# Revit family: Nivellierbare Kassette mit Schnurauslass, RKSNUZD3, 20-25, 9
name_source: partatom
category: Generic Models
revit_build: Autodesk Revit 2015 (Build: 20140606_1530(x64)
units: mm (PartAtom-declared; Revit-internal decimal feet)

## types (4) — shared parameters
Height 1 = 30 mm  [stored 0.0984252 ft]
Length = 243 mm
Manufacturer = OBO Bettermann
URL = http://www.obo-bettermann.com
Width = 243 mm

## per-type parameters (varying)
| type | Cut depth | GTIN | Height | Manufacturer Art.No. | Material |
| RKSN2 UZD3 9VS20 | 20 mm  [stored 0.0656168 ft] | 4012195867302 | 90 mm  [stored 0.295276 ft] | 7409238 | Stainless Steel, Polished |
| RKSN2 UZD3 9MS20 | 20 mm  [stored 0.0656168 ft] | 4012195867289 | 90 mm  [stored 0.295276 ft] | 7409232 | Brass, Soft Yellow, Welded |
| RKSN2 UZD3 9VS25 | 25 mm  [stored 0.082021 ft] | 4012195867333 | 95 mm | 7409240 | Stainless Steel, Polished |
| RKSN2 UZD3 9MS25 | 25 mm  [stored 0.082021 ft] | 4012195867296 | 95 mm | 7409234 | Brass, Soft Yellow, Welded |

note: column(s) folded — value = type name in every type: Article Type

note: [stored X ft] marks values corroborated as IEEE doubles in the binary element streams (Revit-internal decimal feet)

## geometry (parser evidence)
native form markers: Sweep x2
no freeform markers — native parametric forms only
